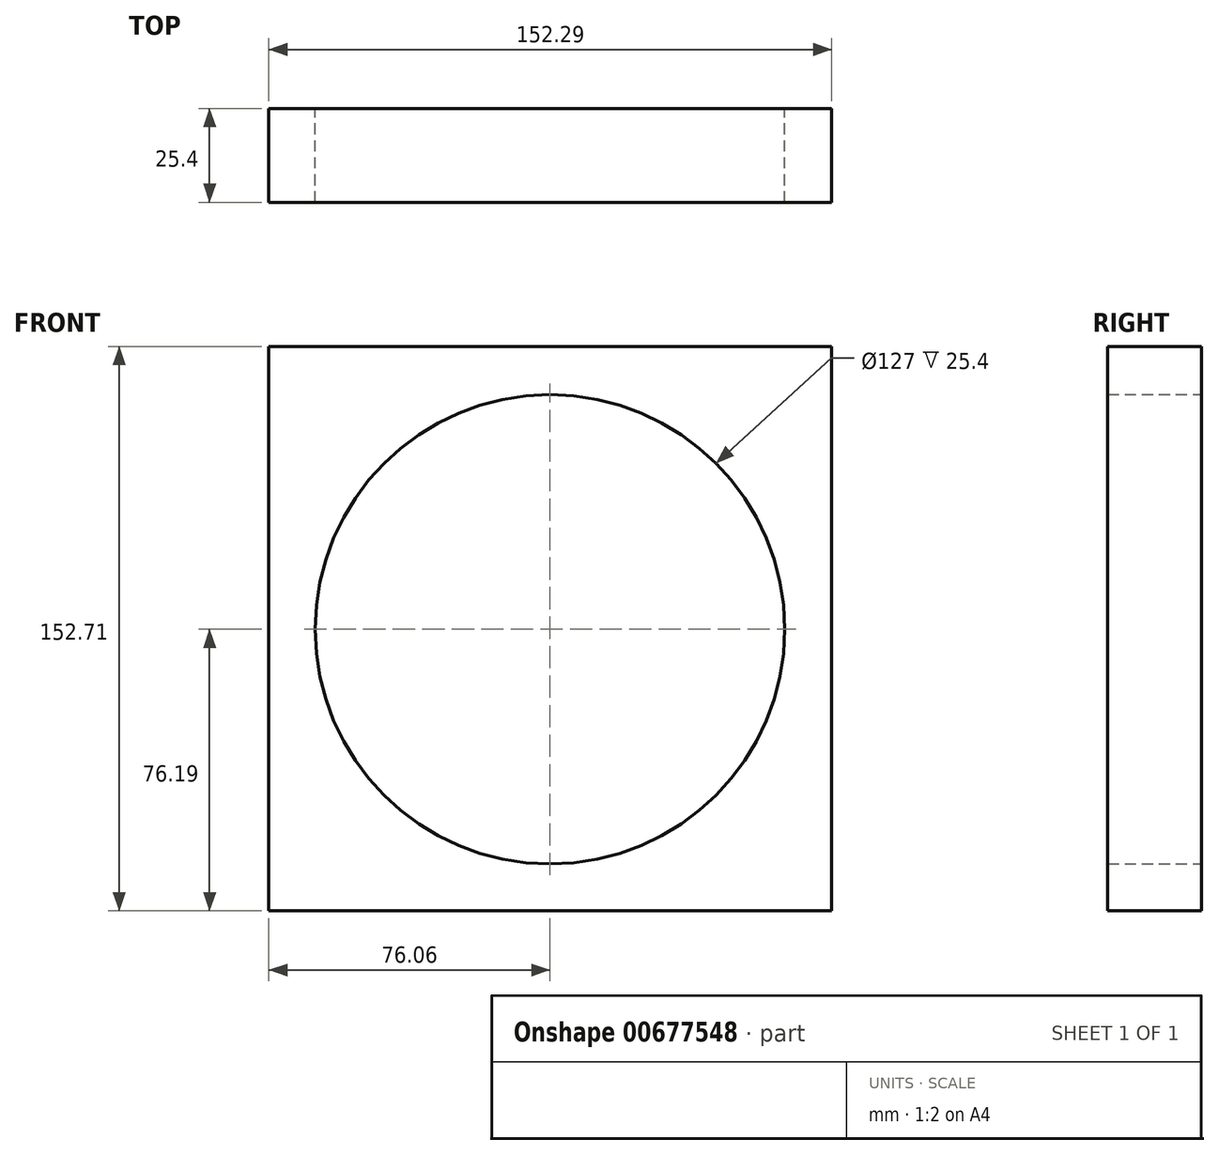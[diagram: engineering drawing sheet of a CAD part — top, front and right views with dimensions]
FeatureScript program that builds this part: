
annotation { "Feature Type Name" : "Feature", "Feature Type Description" : "" }
export const myFeature = defineFeature(function(context is Context, id is Id, definition is map)
    precondition{}
    {
        {
            var Q0;
            Q0=qCreatedBy(makeId("Front.planeOp"),FACE);
            var sketch = newSketch(context, id + "F0", { "sketchPlane" : qUnion([Q0])});
            skCircle(sketch, "E0", {"center": v(0, 0) * mm, "radius": 63.5 * mm});
            skLineSegment(sketch, "E1.bottom", {"start": v(-76.06, 76.52) * mm, "end": v(76.23, 76.52) * mm});
            skLineSegment(sketch, "E1.top", {"start": v(-76.06, -76.19) * mm, "end": v(76.23, -76.19) * mm});
            skLineSegment(sketch, "E1.left", {"start": v(-76.06, 76.52) * mm, "end": v(-76.06, -76.19) * mm});
            skLineSegment(sketch, "E1.right", {"start": v(76.23, 76.52) * mm, "end": v(76.23, -76.19) * mm});
            skSolve(sketch);
        }
        {
            var Q0;
            Q0 = qSketchRegion(id + "F0", true);
            extrude(context, id + "F1", {"entities" : qUnion([Q0]), "depth" : 25.4 * mm, "offsetDistance" : 25.4 * mm});
        }
    });
